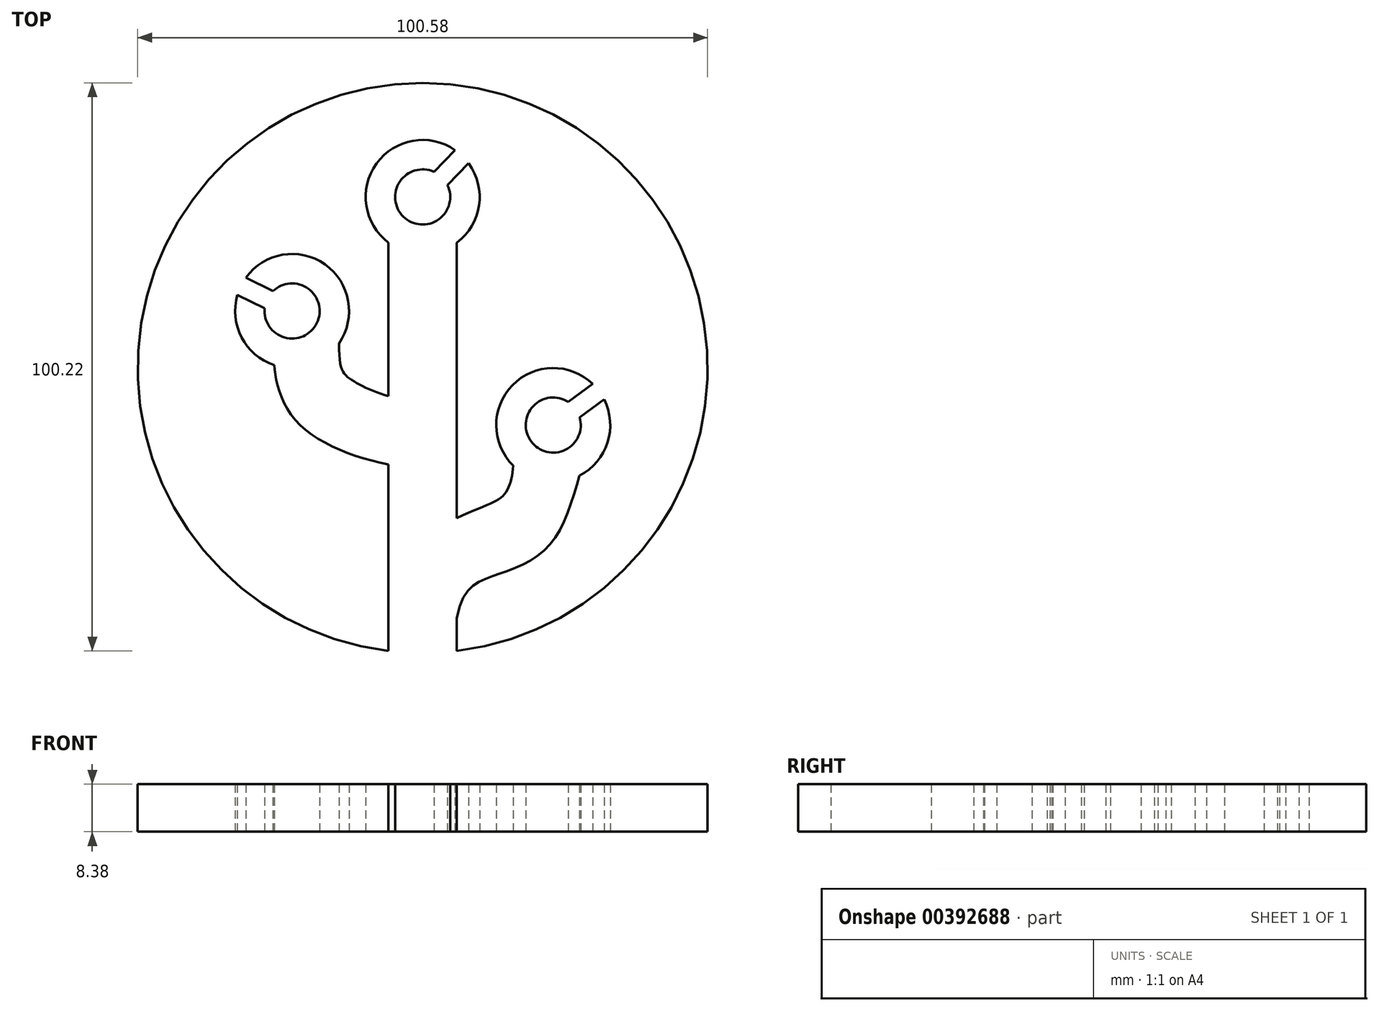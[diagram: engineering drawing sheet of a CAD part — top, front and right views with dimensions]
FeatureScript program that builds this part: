
annotation { "Feature Type Name" : "Feature", "Feature Type Description" : "" }
export const myFeature = defineFeature(function(context is Context, id is Id, definition is map)
    precondition{}
    {
        {
            var Q0;
            Q0=qCreatedBy(makeId("Top.planeOp"),FACE);
            var sketch = newSketch(context, id + "F0", { "sketchPlane" : qUnion([Q0])});
            skCircle(sketch, "E0", {"center": v(0, 0) * mm, "radius": 76.2 * mm});
            skLineSegment(sketch, "E1.bottom", {"start": v(-9.14, 33.53) * mm, "end": v(9.14, 33.53) * mm});
            skLineSegment(sketch, "E1.top", {"start": v(-9.14, -75.65) * mm, "end": v(9.14, -75.65) * mm});
            skLineSegment(sketch, "E1.left", {"start": v(-9.14, 33.53) * mm, "end": v(-9.14, -75.65) * mm});
            skLineSegment(sketch, "E1.right", {"start": v(9.14, 33.53) * mm, "end": v(9.14, -75.65) * mm});
            skCircle(sketch, "E2", {"center": v(0, 45.72) * mm, "radius": 15.24 * mm});
            skCircle(sketch, "E3", {"center": v(0, 45.72) * mm, "radius": 7.37 * mm});
            skCircle(sketch, "E4", {"center": v(-34.92, 15.24) * mm, "radius": 15.24 * mm});
            skCircle(sketch, "E5", {"center": v(-34.92, 15.24) * mm, "radius": 7.37 * mm});
            skCircle(sketch, "E6", {"center": v(34.92, -15.24) * mm, "radius": 15.24 * mm});
            skCircle(sketch, "E7", {"center": v(34.92, -15.24) * mm, "radius": 7.37 * mm});
            skFitSpline(sketch, "E8", {"points": [v(-39.72, 0.78) * mm, v(-34.32, -13.57) * mm, v(-9.14, -25.81) * mm], "startDerivative": vector(1.93, -25.06) * mm, "endDerivative": vector(51.14, -10.84) * mm});
            skFitSpline(sketch, "E9", {"points": [v(-22.38, 6.58) * mm, v(-19.56, -2.78) * mm, v(-9.14, -7.53) * mm], "startDerivative": vector(0.23, -41.12) * mm, "endDerivative": vector(25.5, -7.48) * mm});
            skFitSpline(sketch, "E10", {"points": [v(41.93, -28.77) * mm, v(33.38, -47.9) * mm, v(18.94, -55.56) * mm, v(9.14, -66.93) * mm], "startDerivative": vector(-16.43, -57.7) * mm, "endDerivative": vector(-13.53, -80.51) * mm});
            skFitSpline(sketch, "E11", {"points": [v(24.24, -26.11) * mm, v(22.02, -33.57) * mm, v(9.14, -40.11) * mm], "startDerivative": vector(-1.88, -20.59) * mm, "endDerivative": vector(-38.99, -18.38) * mm});
            skLineSegment(sketch, "E12", {"start": v(10.64, 56.63) * mm, "end": v(5.14, 51) * mm});
            skLineSegment(sketch, "E13", {"start": v(-10.64, 34.8) * mm, "end": v(-5.14, 40.45) * mm});
            skLineSegment(sketch, "E14", {"start": v(-10.91, 56.36) * mm, "end": v(-5.27, 50.86) * mm});
            skLineSegment(sketch, "E15", {"start": v(10.91, 35.08) * mm, "end": v(5.27, 40.58) * mm});
            skLineSegment(sketch, "E16", {"start": v(25.85, -2.99) * mm, "end": v(30.54, -9.32) * mm});
            skLineSegment(sketch, "E17", {"start": v(47.17, -6.17) * mm, "end": v(40.84, -10.86) * mm});
            skLineSegment(sketch, "E18", {"start": v(43.99, -27.5) * mm, "end": v(39.3, -21.16) * mm});
            skLineSegment(sketch, "E19", {"start": v(22.67, -24.3) * mm, "end": v(29, -19.62) * mm});
            skLineSegment(sketch, "E20", {"start": v(-48.61, 21.93) * mm, "end": v(-41.54, 18.47) * mm});
            skLineSegment(sketch, "E21", {"start": v(-41.6, 1.55) * mm, "end": v(-38.15, 8.62) * mm});
            skLineSegment(sketch, "E22", {"start": v(-21.22, 8.55) * mm, "end": v(-28.3, 12) * mm});
            skLineSegment(sketch, "E23", {"start": v(-28.23, 28.93) * mm, "end": v(-31.69, 21.86) * mm});
            skLineSegment(sketch, "E24", {"start": v(-48.61, 21.93) * mm, "end": v(-49.73, 19.65) * mm});
            skLineSegment(sketch, "E25", {"start": v(-49.73, 19.65) * mm, "end": v(-40.6, 15.19) * mm});
            skLineSegment(sketch, "E26.MirrorCS", {"start": v(-47.5, 24.2) * mm, "end": v(-38.37, 19.75) * mm});
            skLineSegment(sketch, "E27.MirrorCS", {"start": v(-48.61, 21.93) * mm, "end": v(-47.5, 24.2) * mm});
            skLineSegment(sketch, "E28", {"start": v(10.64, 56.63) * mm, "end": v(8.82, 58.4) * mm});
            skLineSegment(sketch, "E29", {"start": v(8.82, 58.4) * mm, "end": v(-1.52, 47.8) * mm});
            skLineSegment(sketch, "E30.MirrorCS", {"start": v(10.64, 56.63) * mm, "end": v(12.46, 54.86) * mm});
            skLineSegment(sketch, "E31.MirrorCS", {"start": v(12.46, 54.86) * mm, "end": v(2.11, 44.25) * mm});
            skLineSegment(sketch, "E32", {"start": v(47.17, -6.17) * mm, "end": v(45.66, -4.13) * mm});
            skLineSegment(sketch, "E33", {"start": v(45.66, -4.13) * mm, "end": v(37.98, -9.81) * mm});
            skLineSegment(sketch, "E34.MirrorCS", {"start": v(48.68, -8.22) * mm, "end": v(41, -13.9) * mm});
            skLineSegment(sketch, "E35.MirrorCS", {"start": v(47.17, -6.17) * mm, "end": v(48.68, -8.22) * mm});
            skSolve(sketch);
        }
        {
            var Q0;
            {var subQ1=sQuery(id+"F0.wireOp",EDGE,"E8");Q0=makeQuery(id+"F0.imprint","IMPRINT",FACE,{"disambiguationData":[TD([[makeQuery(id+"F0.imprint","IMPRINT",EDGE,{"derivedFrom":subQ1}),-1.0]])]});}
            var Q1;
            {var subQ0=sQuery(id+"F0.wireOp",EDGE,"E5");var subQ1=makeQuery(id+"F0.imprint","INTERSECT",VERTEX,{"derivedFrom":[subQ0,sQuery(id+"F0.wireOp",EDGE,"E20")]});Q1=makeQuery(id+"F0.imprint","IMPRINT",FACE,{"disambiguationData":[TD([[makeQuery(id+"F0.imprint","IMPRINT",EDGE,{"disambiguationData":[TD([[subQ1,1.0]])],"derivedFrom":subQ0}),1.0]])]});}
            var Q2;
            {var subQ0=sQuery(id+"F0.wireOp",EDGE,"E3");var subQ1=makeQuery(id+"F0.imprint","INTERSECT",VERTEX,{"derivedFrom":[subQ0,sQuery(id+"F0.wireOp",EDGE,"E12")]});Q2=makeQuery(id+"F0.imprint","IMPRINT",FACE,{"disambiguationData":[TD([[makeQuery(id+"F0.imprint","IMPRINT",EDGE,{"disambiguationData":[TD([[subQ1,-1.0]])],"derivedFrom":subQ0}),1.0]])]});}
            var Q3;
            {var subQ0=sQuery(id+"F0.wireOp",EDGE,"E7");var subQ1=makeQuery(id+"F0.imprint","INTERSECT",VERTEX,{"derivedFrom":[subQ0,sQuery(id+"F0.wireOp",EDGE,"E16")]});Q3=makeQuery(id+"F0.imprint","IMPRINT",FACE,{"disambiguationData":[TD([[makeQuery(id+"F0.imprint","IMPRINT",EDGE,{"disambiguationData":[TD([[subQ1,1.0]])],"derivedFrom":subQ0}),1.0]])]});}
            var Q4;
            {var subQ0=sQuery(id+"F0.wireOp",EDGE,"E20");Q4=makeQuery(id+"F0.imprint","IMPRINT",FACE,{"disambiguationData":[TD([[makeQuery(id+"F0.imprint","IMPRINT",EDGE,{"derivedFrom":subQ0}),-1.0]])]});}
            var Q5;
            {var subQ0=sQuery(id+"F0.wireOp",EDGE,"E17");Q5=makeQuery(id+"F0.imprint","IMPRINT",FACE,{"disambiguationData":[TD([[makeQuery(id+"F0.imprint","IMPRINT",EDGE,{"derivedFrom":subQ0}),-1.0]])]});}
            var Q6;
            {var subQ0=sQuery(id+"F0.wireOp",EDGE,"E17");Q6=makeQuery(id+"F0.imprint","IMPRINT",FACE,{"disambiguationData":[TD([[makeQuery(id+"F0.imprint","IMPRINT",EDGE,{"derivedFrom":subQ0}),1.0]])]});}
            var Q7;
            {var subQ0=sQuery(id+"F0.wireOp",EDGE,"E12");Q7=makeQuery(id+"F0.imprint","IMPRINT",FACE,{"disambiguationData":[TD([[makeQuery(id+"F0.imprint","IMPRINT",EDGE,{"derivedFrom":subQ0}),1.0]])]});}
            var Q8;
            {var subQ0=sQuery(id+"F0.wireOp",EDGE,"E12");Q8=makeQuery(id+"F0.imprint","IMPRINT",FACE,{"disambiguationData":[TD([[makeQuery(id+"F0.imprint","IMPRINT",EDGE,{"derivedFrom":subQ0}),-1.0]])]});}
            var Q9;
            {var subQ0=sQuery(id+"F0.wireOp",EDGE,"E20");Q9=makeQuery(id+"F0.imprint","IMPRINT",FACE,{"disambiguationData":[TD([[makeQuery(id+"F0.imprint","IMPRINT",EDGE,{"derivedFrom":subQ0}),1.0]])]});}
            var Q10;
            {var subQ0=sQuery(id+"F0.wireOp",EDGE,"E35.MirrorCS");Q10=makeQuery(id+"F0.imprint","IMPRINT",FACE,{"disambiguationData":[TD([[makeQuery(id+"F0.imprint","IMPRINT",EDGE,{"derivedFrom":subQ0}),-1.0]])]});}
            var Q11;
            {var subQ0=sQuery(id+"F0.wireOp",EDGE,"E32");Q11=makeQuery(id+"F0.imprint","IMPRINT",FACE,{"disambiguationData":[TD([[makeQuery(id+"F0.imprint","IMPRINT",EDGE,{"derivedFrom":subQ0}),1.0]])]});}
            var Q12;
            {var subQ0=sQuery(id+"F0.wireOp",EDGE,"E28");Q12=makeQuery(id+"F0.imprint","IMPRINT",FACE,{"disambiguationData":[TD([[makeQuery(id+"F0.imprint","IMPRINT",EDGE,{"derivedFrom":subQ0}),1.0]])]});}
            var Q13;
            {var subQ0=sQuery(id+"F0.wireOp",EDGE,"E30.MirrorCS");Q13=makeQuery(id+"F0.imprint","IMPRINT",FACE,{"disambiguationData":[TD([[makeQuery(id+"F0.imprint","IMPRINT",EDGE,{"derivedFrom":subQ0}),-1.0]])]});}
            var Q14;
            {var subQ0=sQuery(id+"F0.wireOp",EDGE,"E24");Q14=makeQuery(id+"F0.imprint","IMPRINT",FACE,{"disambiguationData":[TD([[makeQuery(id+"F0.imprint","IMPRINT",EDGE,{"derivedFrom":subQ0}),1.0]])]});}
            var Q15;
            {var subQ0=sQuery(id+"F0.wireOp",EDGE,"E27.MirrorCS");Q15=makeQuery(id+"F0.imprint","IMPRINT",FACE,{"disambiguationData":[TD([[makeQuery(id+"F0.imprint","IMPRINT",EDGE,{"derivedFrom":subQ0}),-1.0]])]});}
            extrude(context, id + "F1", {"entities" : qUnion([Q0, Q1, Q2, Q3, Q4, Q5, Q6, Q7, Q8, Q9, Q10, Q11, Q12, Q13, Q14, Q15]), "depth" : 12.7 * mm});
        }
        {
            var Q0;
            Q0=makeQuery(id+"F1.opExtrude","SWEPT_BODY",BODY,{"disambiguationData":[OSD([sQuery(id+"F0.wireOp",EDGE,"E0"),sQuery(id+"F0.wireOp",EDGE,"E1.left"),sQuery(id+"F0.wireOp",EDGE,"E1.right"),sQuery(id+"F0.wireOp",EDGE,"E2"),sQuery(id+"F0.wireOp",EDGE,"E3"),sQuery(id+"F0.wireOp",EDGE,"E4"),sQuery(id+"F0.wireOp",EDGE,"E5"),sQuery(id+"F0.wireOp",EDGE,"E6"),sQuery(id+"F0.wireOp",EDGE,"E7"),sQuery(id+"F0.wireOp",EDGE,"E8"),sQuery(id+"F0.wireOp",EDGE,"E9"),sQuery(id+"F0.wireOp",EDGE,"E10"),sQuery(id+"F0.wireOp",EDGE,"E11"),sQuery(id+"F0.wireOp",EDGE,"E25"),sQuery(id+"F0.wireOp",EDGE,"E26.MirrorCS"),sQuery(id+"F0.wireOp",EDGE,"E29"),sQuery(id+"F0.wireOp",EDGE,"E31.MirrorCS"),sQuery(id+"F0.wireOp",EDGE,"E33"),sQuery(id+"F0.wireOp",EDGE,"E34.MirrorCS")])]});
            var Q1;
            Q1=qCreatedBy(makeId("Origin.pointOp"),VERTEX);
            transform(context, id + "F2", {"entities" : qUnion([Q0]), "transformType" : TransformType.SCALE_UNIFORMLY, "scale" : 0.66, "scalePoint" : qUnion([Q1]), "makeCopy" : false});
        }
    });
